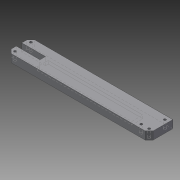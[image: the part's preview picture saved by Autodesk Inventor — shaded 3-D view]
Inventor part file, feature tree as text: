
AUTODESK INVENTOR PART (.ipt)
format: ipt  version: 2015 (Build 190159000, 159)  size: 130,048 bytes
history: native  units: mm
features: sketch x5, extrude x3, hole x2, chamfer x2
ambient origin geometry x8: Origin, YZ Plane, XZ Plane, XY Plane, X Axis, Y Axis, Z Axis, Center Point
bodies: Solid1 (feature_tree)
feature tree (12):
  extrude  "Extrusion1"  Depth=30.0mm
  hole  "Hole1"  [1 undecoded]
  chamfer  "Chamfer1"  Distance=5.0mm Angle=45.0deg
  extrude  "Extrusion2"  Depth=10.0mm
  extrude  "Extrusion3"  Depth=10.0mm
  hole  "Hole2"  [1 undecoded]
  chamfer  "Chamfer2"  Distance=10.0mm
  sketch  "Sketch1"  dims[d0=180.0mm d1=30.0mm]
  sketch  "Sketch2"  dims[d2=10.0mm d3=0.0mm d4=5.0mm]
  sketch  "Sketch3"  dims[d5=5.0mm]
  sketch  "Sketch4"  dims[d6=5.0mm]
  sketch  "Sketch5"  dims[d7=5.0mm d8=3.0mm d9=6.0mm d10=4.0mm d11=2.0mm d12=90.0deg d13=10.0mm d14=20.594885mm d15=5.0mm d16=2.0mm d17=45.0deg d18=5.0mm d19=5.0mm d20=30.0mm d21=10.0mm d22=0.0mm d23=8.0mm d24=8.0mm d25=30.0mm d26=4.0mm d27=0.0mm d28=5.0mm d29=5.0mm d30=5.0mm d31=5.0mm d32=5.0mm d33=10.0mm d34=3.0mm d35=6.0mm d36=4.0mm d37=2.0mm d38=90.0deg d39=10.0mm d40=20.594885mm d41=5.0mm d42=2.0mm d43=45.0deg]
note: 2 required parameter values undecoded (feature->parameter linkage not recoverable at this tier; creation-order binding heuristic only, values carry confidence <= 0.55)
